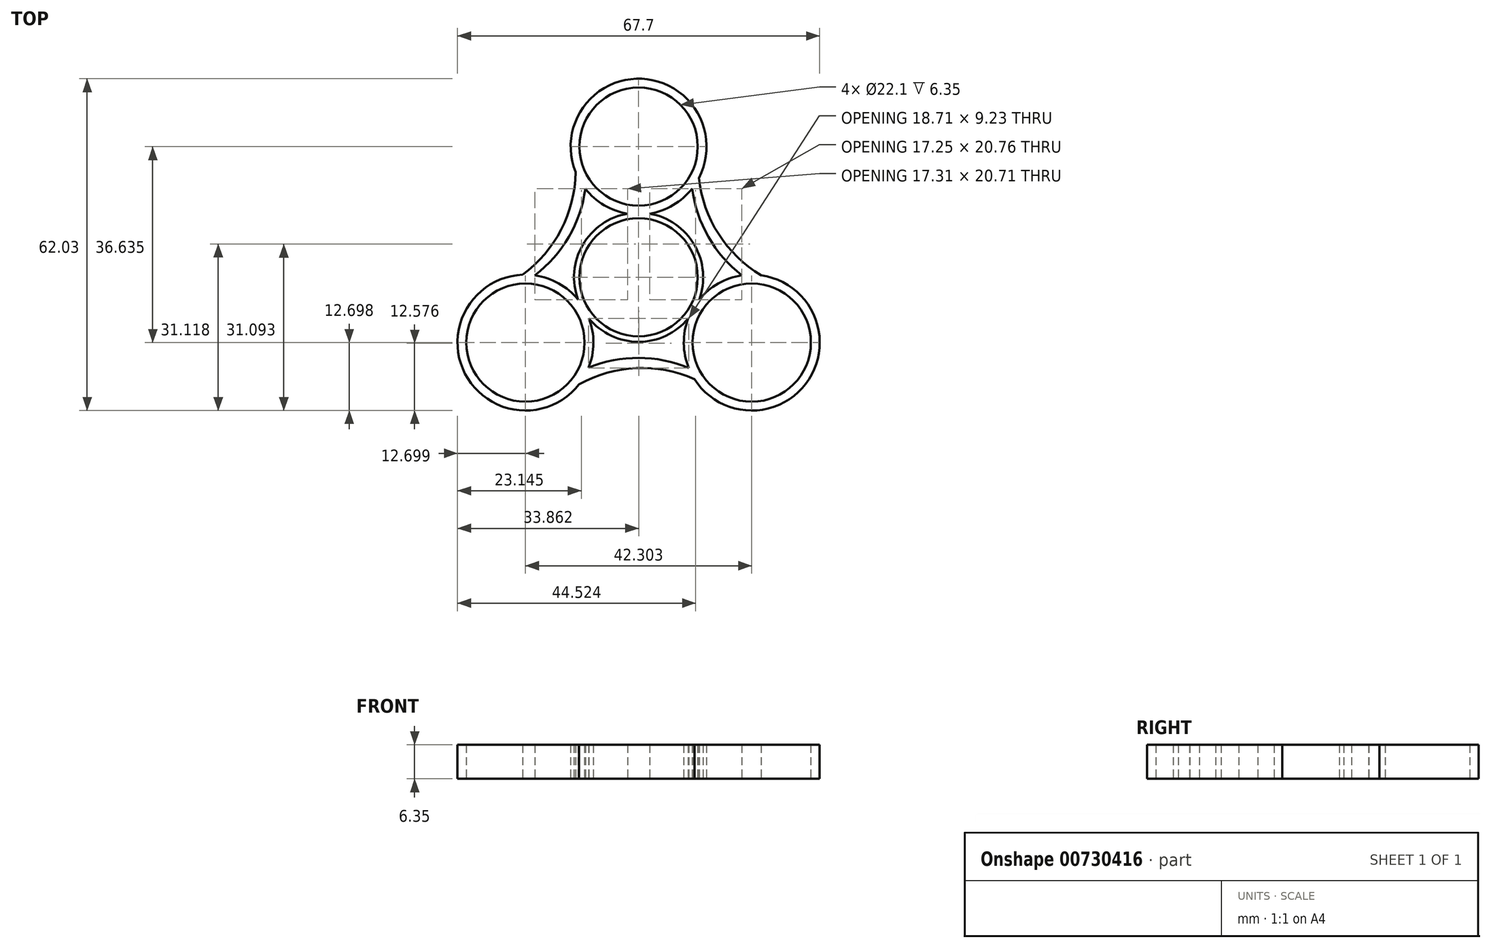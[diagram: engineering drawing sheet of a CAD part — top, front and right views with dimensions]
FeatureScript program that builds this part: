
annotation { "Feature Type Name" : "Feature", "Feature Type Description" : "" }
export const myFeature = defineFeature(function(context is Context, id is Id, definition is map)
    precondition{}
    {
        {
            var Q0;
            Q0=qCreatedBy(makeId("Top.planeOp"),FACE);
            var sketch = newSketch(context, id + "F0", { "sketchPlane" : qUnion([Q0])});
            skCircle(sketch, "E0", {"center": v(0, 0) * mm, "radius": 11.05 * mm});
            skArc(sketch, "E1", {"start": v(-2.05, 11.89) * mm, "mid": v(-10.45, 6.03) * mm, "end": v(-11.32, -4.17) * mm});
            skCircle(sketch, "E2", {"center": v(0, 24.42) * mm, "radius": 11.05 * mm});
            skArc(sketch, "E3", {"start": v(2.05, 11.89) * mm, "mid": v(6.46, 13.5) * mm, "end": v(10, 16.59) * mm});
            skArc(sketch, "E4.1.0", {"start": v(-11.32, -4.17) * mm, "mid": v(-14.92, -1.15) * mm, "end": v(-19.36, 0.36) * mm});
            skCircle(sketch, "E4.1.1", {"center": v(-21.15, -12.21) * mm, "radius": 11.05 * mm});
            skArc(sketch, "E4.2.0", {"start": v(9.27, -7.72) * mm, "mid": v(8.45, -12.34) * mm, "end": v(9.37, -16.95) * mm});
            skCircle(sketch, "E4.2.1", {"center": v(21.15, -12.21) * mm, "radius": 11.05 * mm});
            skArc(sketch, "E5.trimOffspring", {"start": v(-9.27, -7.72) * mm, "mid": v(0, -12.06) * mm, "end": v(9.27, -7.72) * mm});
            skArc(sketch, "E6.trimOffspring", {"start": v(11.32, -4.17) * mm, "mid": v(10.45, 6.03) * mm, "end": v(2.05, 11.89) * mm});
            skArc(sketch, "E7", {"start": v(-21.7, 0.48) * mm, "mid": v(-14.48, 8.9) * mm, "end": v(-11.77, 19.66) * mm});
            skArc(sketch, "E8", {"start": v(-19.36, 0.36) * mm, "mid": v(-13.06, 7.52) * mm, "end": v(-9.95, 16.54) * mm});
            skArc(sketch, "E9.trimOffspring", {"start": v(-9.95, 16.54) * mm, "mid": v(-6.44, 13.47) * mm, "end": v(-2.05, 11.89) * mm});
            skArc(sketch, "E10.trimOffspring", {"start": v(-21.7, 0.48) * mm, "mid": v(-32.44, -18.03) * mm, "end": v(-11.14, -20.02) * mm});
            skArc(sketch, "E11.1.0", {"start": v(9.37, -16.95) * mm, "mid": v(0.02, -15.07) * mm, "end": v(-9.34, -16.89) * mm});
            skArc(sketch, "E11.1.1", {"start": v(10.44, -19.03) * mm, "mid": v(-0.47, -16.99) * mm, "end": v(-11.14, -20.02) * mm});
            skArc(sketch, "E11.2.0", {"start": v(10, 16.59) * mm, "mid": v(13.05, 7.55) * mm, "end": v(19.3, 0.35) * mm});
            skArc(sketch, "E11.2.1", {"start": v(11.26, 18.55) * mm, "mid": v(14.94, 8.09) * mm, "end": v(22.9, 0.37) * mm});
            skArc(sketch, "E12.trimOffspring", {"start": v(11.26, 18.55) * mm, "mid": v(0.6, 37.1) * mm, "end": v(-11.77, 19.66) * mm});
            skArc(sketch, "E13.trimOffspring", {"start": v(19.3, 0.35) * mm, "mid": v(14.89, -1.16) * mm, "end": v(11.32, -4.17) * mm});
            skArc(sketch, "E14.trimOffspring", {"start": v(10.44, -19.03) * mm, "mid": v(31.83, -19.08) * mm, "end": v(22.9, 0.37) * mm});
            skArc(sketch, "E15.trimOffspring", {"start": v(-9.34, -16.89) * mm, "mid": v(-8.45, -12.31) * mm, "end": v(-9.27, -7.72) * mm});
            skSolve(sketch);
        }
        {
            var Q0;
            Q0 = qSketchRegion(id + "F0", true);
            extrude(context, id + "F1", {"entities" : qUnion([Q0]), "depth" : 6.35 * mm, "offsetDistance" : 25.4 * mm});
        }
    });
